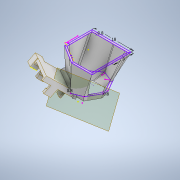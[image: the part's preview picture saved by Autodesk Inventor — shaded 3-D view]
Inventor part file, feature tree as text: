
AUTODESK INVENTOR PART (.ipt)
format: ipt  version: 2022 (Build 260153000, 153)  size: 530,432 bytes
history: native  units: in
note: dims shown in document units (in); Inventor stores cm internally (conversion verified against a paired STEP export)
features: sketch x10, plane x5, other x4, loft x4, extrude x1, split x1, move_body x1, revolve x1
ambient origin geometry x8: Origin, YZ Plane, XZ Plane, XY Plane, X Axis, Y Axis, Z Axis, Center Point
bodies: Solid1 (feature_tree)
feature tree (27):
  sketch  "Sketch1"  dims[d0=0.2441in d1=60.0deg]
  plane  "Work Plane1"
  plane  "Work Plane2"
  sketch  "Sketch2"  dims[d2=0.1063in d3=0.202in]
  other  "Repaired Geometry1"
  extrude  "Extrusion3"  TaperAngle=60.0deg  [1 undecoded]
  plane  "Work Plane5"
  sketch  "Sketch4"  dims[d8=0.0315in d11=0.1181in]
  plane  "Work Plane3"
  split  "Split3"
  sketch  "Sketch5"  dims[d14=0.0315in d15=0.0315in]
  plane  "Work Plane4"
  sketch  "Sketch6"  dims[d20=0.1181in d27=0.1181in d28=0.1181in d29=0.0in d30=0.0in]
  loft  "Loft3"
  other  "cam_holder_new_module"
  sketch  "Sketch7"  dims[d33=0.3937in]
  loft  "Loft5"
  move_body  "Move Body3"
  sketch  "Sketch9"  dims[d36=0.0315in]
  revolve  "Revolution1"  [1 undecoded]
  loft  "Loft9"
  loft  "Loft10"
  sketch  "Sketch11"  dims[d44=0.3543in d45=0.7087in d48=0.0315in d57=0.0in d58=90.0deg d59=0.0in d60=90.0deg d73=0.0933in d74=0.0315in d75=0.0984in d76=0.0591in d77=0.0591in d78=0.0in d79=90.0deg d80=0.0in d81=90.0deg d84=30.0deg d88=-0.3436in d89=-0.3125in d90=0.0394in d91=-0.1535in d100=0.3779in d105=0.0in d106=90.0deg d107=0.0in d108=90.0deg d109=0.0in d110=90.0deg d111=0.0in d112=90.0deg d101=0.0197in d102=0.0344in d103=0.0197in d104=0.0344in]
  sketch  "Sketch3"  dims[d4=0.1181in d7=0.0315in]
  sketch  "Sketch10"  dims[d40=0.6299in]
  other  "Composite1"
  other  "Srf1"
note: 2 required parameter values undecoded (feature->parameter linkage not recoverable at this tier; creation-order binding heuristic only, values carry confidence <= 0.55)